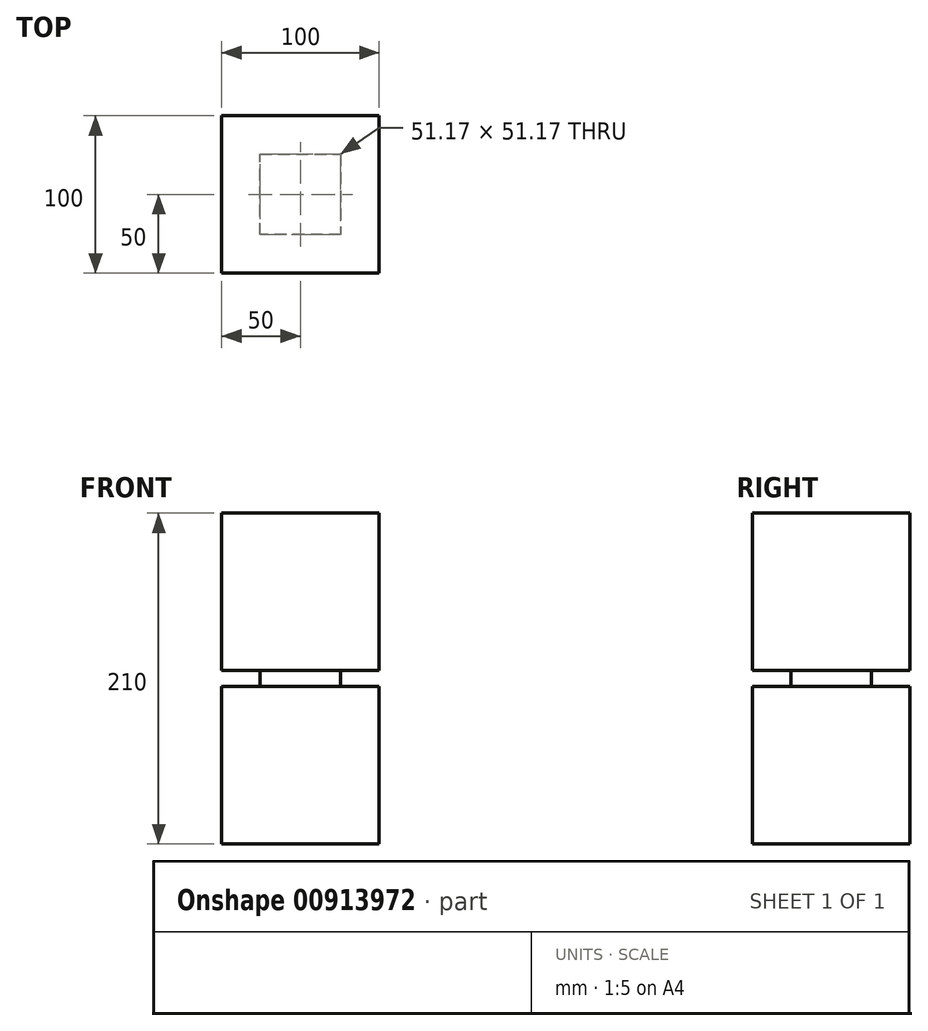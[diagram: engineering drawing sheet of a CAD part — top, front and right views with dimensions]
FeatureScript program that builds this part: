
annotation { "Feature Type Name" : "Feature", "Feature Type Description" : "" }
export const myFeature = defineFeature(function(context is Context, id is Id, definition is map)
    precondition{}
    {
        {
            var Q0;
            Q0=qCreatedBy(makeId("Top.planeOp"),FACE);
            var sketch = newSketch(context, id + "F0", { "sketchPlane" : qUnion([Q0])});
            skCircle(sketch, "E0.cCircle", {"center": v(0, 0) * mm, "radius": 50 * mm, "construction": true});
            skLineSegment(sketch, "E0.0", {"start": v(50, 50) * mm, "end": v(50, -50) * mm});
            skLineSegment(sketch, "E0.1", {"start": v(50, -50) * mm, "end": v(-50, -50) * mm});
            skLineSegment(sketch, "E0.2", {"start": v(-50, -50) * mm, "end": v(-50, 50) * mm});
            skLineSegment(sketch, "E0.3", {"start": v(-50, 50) * mm, "end": v(50, 50) * mm});
            skPoint(sketch, "E0.0.midPoint", {"position": v(50, 0) * mm});
            skSolve(sketch);
        }
        {
            var Q0;
            Q0=makeQuery(id+"F0.imprint","IMPRINT",FACE,{"disambiguationData":[TD([[makeQuery(id+"F0.imprint","IMPRINT",EDGE,{"derivedFrom":sQuery(id+"F0.wireOp",EDGE,"E0.0")}),-1.0]])]});
            extrude(context, id + "F1", {"entities" : qUnion([Q0]), "depth" : 100 * mm, "offsetDistance" : 25 * mm});
        }
        {
            var Q0;
            Q0=makeQuery(id+"F1.opExtrude","CAP_FACE",FACE,{"disambiguationData":[OSD([sQuery(id+"F0.wireOp",EDGE,"E0.0"),sQuery(id+"F0.wireOp",EDGE,"E0.1"),sQuery(id+"F0.wireOp",EDGE,"E0.2"),sQuery(id+"F0.wireOp",EDGE,"E0.3")])],"isStart":false});
            var sketch = newSketch(context, id + "F2", { "sketchPlane" : qUnion([Q0])});
            skCircle(sketch, "E1.cCircle", {"center": v(0, 0) * mm, "radius": 25.58 * mm, "construction": true});
            skLineSegment(sketch, "E1.0", {"start": v(25.58, 25.58) * mm, "end": v(25.58, -25.58) * mm});
            skLineSegment(sketch, "E1.1", {"start": v(25.58, -25.58) * mm, "end": v(-25.58, -25.58) * mm});
            skLineSegment(sketch, "E1.2", {"start": v(-25.58, -25.58) * mm, "end": v(-25.58, 25.58) * mm});
            skLineSegment(sketch, "E1.3", {"start": v(-25.58, 25.58) * mm, "end": v(25.58, 25.58) * mm});
            skPoint(sketch, "E1.0.midPoint", {"position": v(25.58, 0) * mm});
            skSolve(sketch);
        }
        {
            var Q0;
            Q0=makeQuery(id+"F2.imprint","IMPRINT",FACE,{"disambiguationData":[TD([[makeQuery(id+"F2.imprint","IMPRINT",EDGE,{"derivedFrom":sQuery(id+"F2.wireOp",EDGE,"E1.0")}),-1.0]])]});
            extrude(context, id + "F3", {"entities" : qUnion([Q0]), "operationType" : NewBodyOperationType.ADD, "depth" : 10 * mm, "offsetDistance" : 25 * mm});
        }
        {
            var Q0;
            Q0=makeQuery(id+"F3.opExtrude","CAP_FACE",FACE,{"disambiguationData":[OSD([sQuery(id+"F2.wireOp",EDGE,"E1.0"),sQuery(id+"F2.wireOp",EDGE,"E1.1"),sQuery(id+"F2.wireOp",EDGE,"E1.2"),sQuery(id+"F2.wireOp",EDGE,"E1.3")])],"isStart":false});
            var sketch = newSketch(context, id + "F4", { "sketchPlane" : qUnion([Q0])});
            skCircle(sketch, "E2.cCircle", {"center": v(0, 0) * mm, "radius": 50 * mm, "construction": true});
            skLineSegment(sketch, "E2.0", {"start": v(50, 50) * mm, "end": v(50, -50) * mm});
            skLineSegment(sketch, "E2.1", {"start": v(50, -50) * mm, "end": v(-50, -50) * mm});
            skLineSegment(sketch, "E2.2", {"start": v(-50, -50) * mm, "end": v(-50, 50) * mm});
            skLineSegment(sketch, "E2.3", {"start": v(-50, 50) * mm, "end": v(50, 50) * mm});
            skPoint(sketch, "E2.0.midPoint", {"position": v(50, 0) * mm});
            skSolve(sketch);
        }
        {
            var Q0;
            Q0 = qSketchRegion(id + "F4", true);
            extrude(context, id + "F5", {"entities" : qUnion([Q0]), "operationType" : NewBodyOperationType.ADD, "depth" : 100 * mm, "offsetDistance" : 25 * mm});
        }
    });
